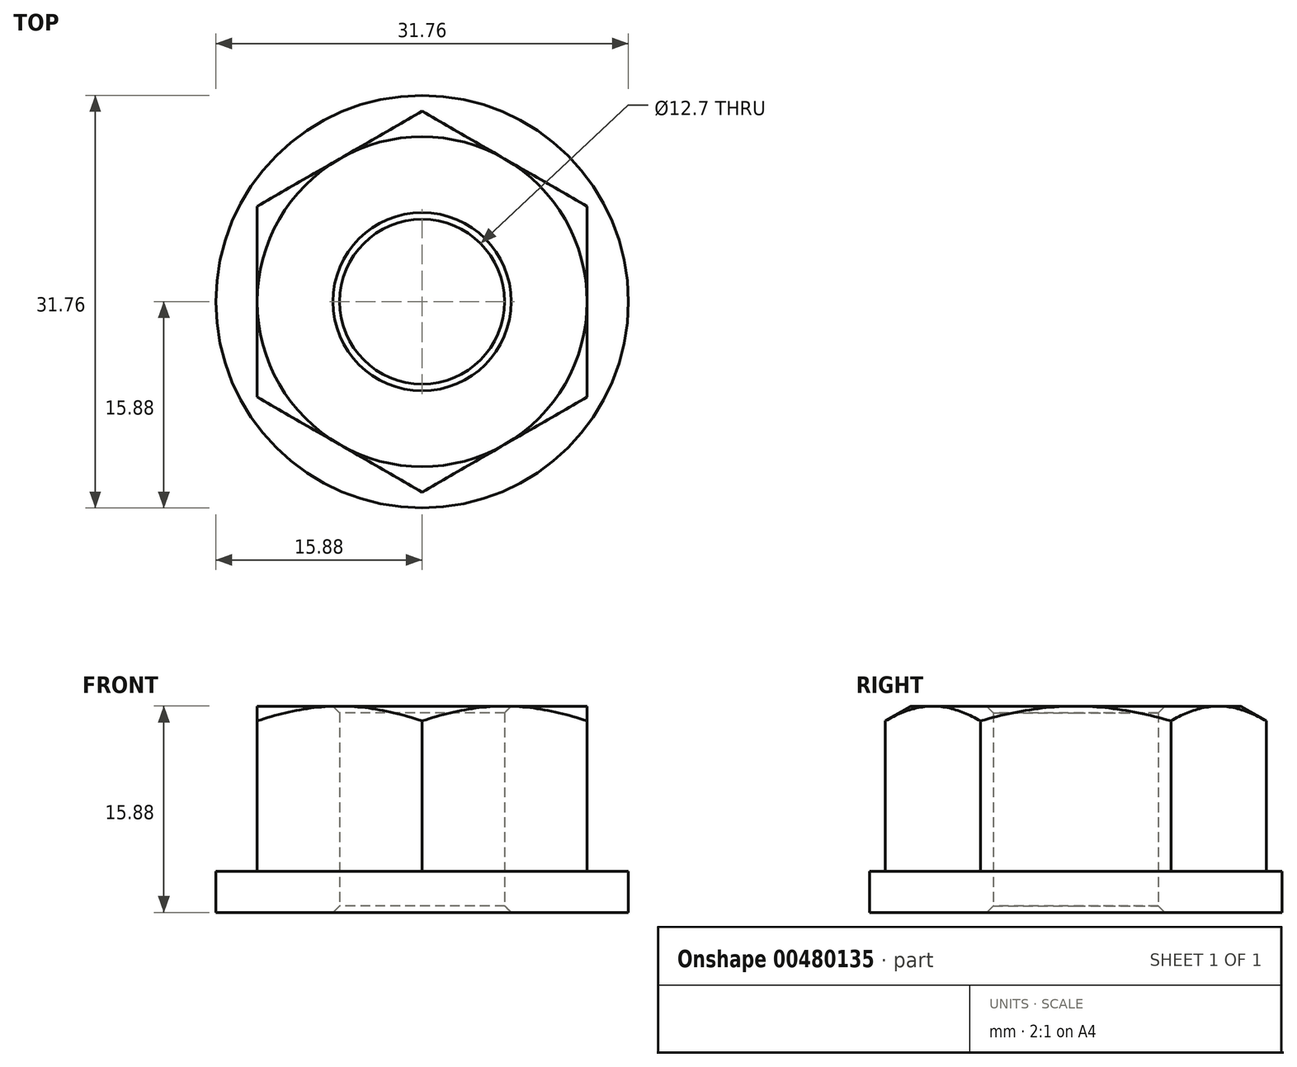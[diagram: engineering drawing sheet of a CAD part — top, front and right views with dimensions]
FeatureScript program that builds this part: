
annotation { "Feature Type Name" : "Feature", "Feature Type Description" : "" }
export const myFeature = defineFeature(function(context is Context, id is Id, definition is map)
    precondition{}
    {
        {
            var Q0;
            Q0=qCreatedBy(makeId("Top.planeOp"),FACE);
            var sketch = newSketch(context, id + "F0", { "sketchPlane" : qUnion([Q0])});
            skCircle(sketch, "E0.cCircle", {"center": v(0, 0) * mm, "radius": 12.7 * mm, "construction": true});
            skLineSegment(sketch, "E0.0", {"start": v(12.7, 7.33) * mm, "end": v(12.7, -7.33) * mm});
            skLineSegment(sketch, "E0.1", {"start": v(12.7, -7.33) * mm, "end": v(0, -14.66) * mm});
            skLineSegment(sketch, "E0.2", {"start": v(0, -14.66) * mm, "end": v(-12.7, -7.33) * mm});
            skLineSegment(sketch, "E0.3", {"start": v(-12.7, -7.33) * mm, "end": v(-12.7, 7.33) * mm});
            skLineSegment(sketch, "E0.4", {"start": v(-12.7, 7.33) * mm, "end": v(0, 14.66) * mm});
            skLineSegment(sketch, "E0.5", {"start": v(0, 14.66) * mm, "end": v(12.7, 7.33) * mm});
            skPoint(sketch, "E0.0.midPoint", {"position": v(12.7, 0) * mm});
            skCircle(sketch, "E1", {"center": v(0, 0) * mm, "radius": 6.35 * mm});
            skSolve(sketch);
        }
        {
            var Q0;
            Q0=makeQuery(id+"F0.imprint","IMPRINT",FACE,{"disambiguationData":[TD([[makeQuery(id+"F0.imprint","IMPRINT",EDGE,{"derivedFrom":sQuery(id+"F0.wireOp",EDGE,"E0.0")}),-1.0]])]});
            extrude(context, id + "F1", {"entities" : qUnion([Q0]), "depth" : 15.88 * mm});
        }
        {
            var Q0;
            Q0=qCreatedBy(makeId("Front.planeOp"),FACE);
            var sketch = newSketch(context, id + "F2", { "sketchPlane" : qUnion([Q0])});
            skLineSegment(sketch, "E2", {"start": v(12.7, 15.88) * mm, "end": v(16.7, 15.88) * mm});
            skLineSegment(sketch, "E3", {"start": v(16.7, 15.88) * mm, "end": v(16.7, 13.56) * mm});
            skLineSegment(sketch, "E4", {"start": v(16.7, 13.56) * mm, "end": v(12.7, 15.88) * mm});
            skLineSegment(sketch, "E5", {"start": v(0, 15.9) * mm, "end": v(0, 0) * mm});
            skSolve(sketch);
        }
        {
            var Q0;
            Q0=makeQuery(id+"F2.imprint","IMPRINT",FACE,{"disambiguationData":[TD([[makeQuery(id+"F2.imprint","IMPRINT",EDGE,{"derivedFrom":sQuery(id+"F2.wireOp",EDGE,"E2")}),-1.0]])]});
            var Q1;
            Q1=sQuery(id+"F2.wireOp",EDGE,"E5");
            revolve(context, id + "F3", {"operationType" : NewBodyOperationType.REMOVE, "entities" : qUnion([Q0]), "axis" : qUnion([Q1]), "revolveType" : RevolveType.FULL, "oppositeDirection" : true});
        }
        {
            var Q0;
            Q0=qCreatedBy(makeId("Top.planeOp"),FACE);
            var sketch = newSketch(context, id + "F4", { "sketchPlane" : qUnion([Q0])});
            skCircle(sketch, "E6", {"center": v(0, 0) * mm, "radius": 15.87 * mm});
            skCircle(sketch, "E7", {"center": v(0, 0) * mm, "radius": 6.35 * mm});
            skSolve(sketch);
        }
        {
            var Q0;
            Q0 = qSketchRegion(id + "F4", true);
            extrude(context, id + "F5", {"entities" : qUnion([Q0]), "operationType" : NewBodyOperationType.ADD, "depth" : 3.17 * mm});
        }
        {
            var Q0;
            Q0=makeQuery(id+"F1.opExtrude","CAP_EDGE",EDGE,{"disambiguationData":[OSD([sQuery(id+"F0.wireOp",EDGE,"E1")])],"isStart":true});
            var Q1;
            Q1=makeQuery(id+"F1.opExtrude","CAP_EDGE",EDGE,{"disambiguationData":[OSD([sQuery(id+"F0.wireOp",EDGE,"E1")])],"isStart":false});
            chamfer(context, id + "F6", {"entities" : qUnion([Q0, Q1]), "width" : 0.5 * mm, "tangentPropagation" : true});
        }
    });
